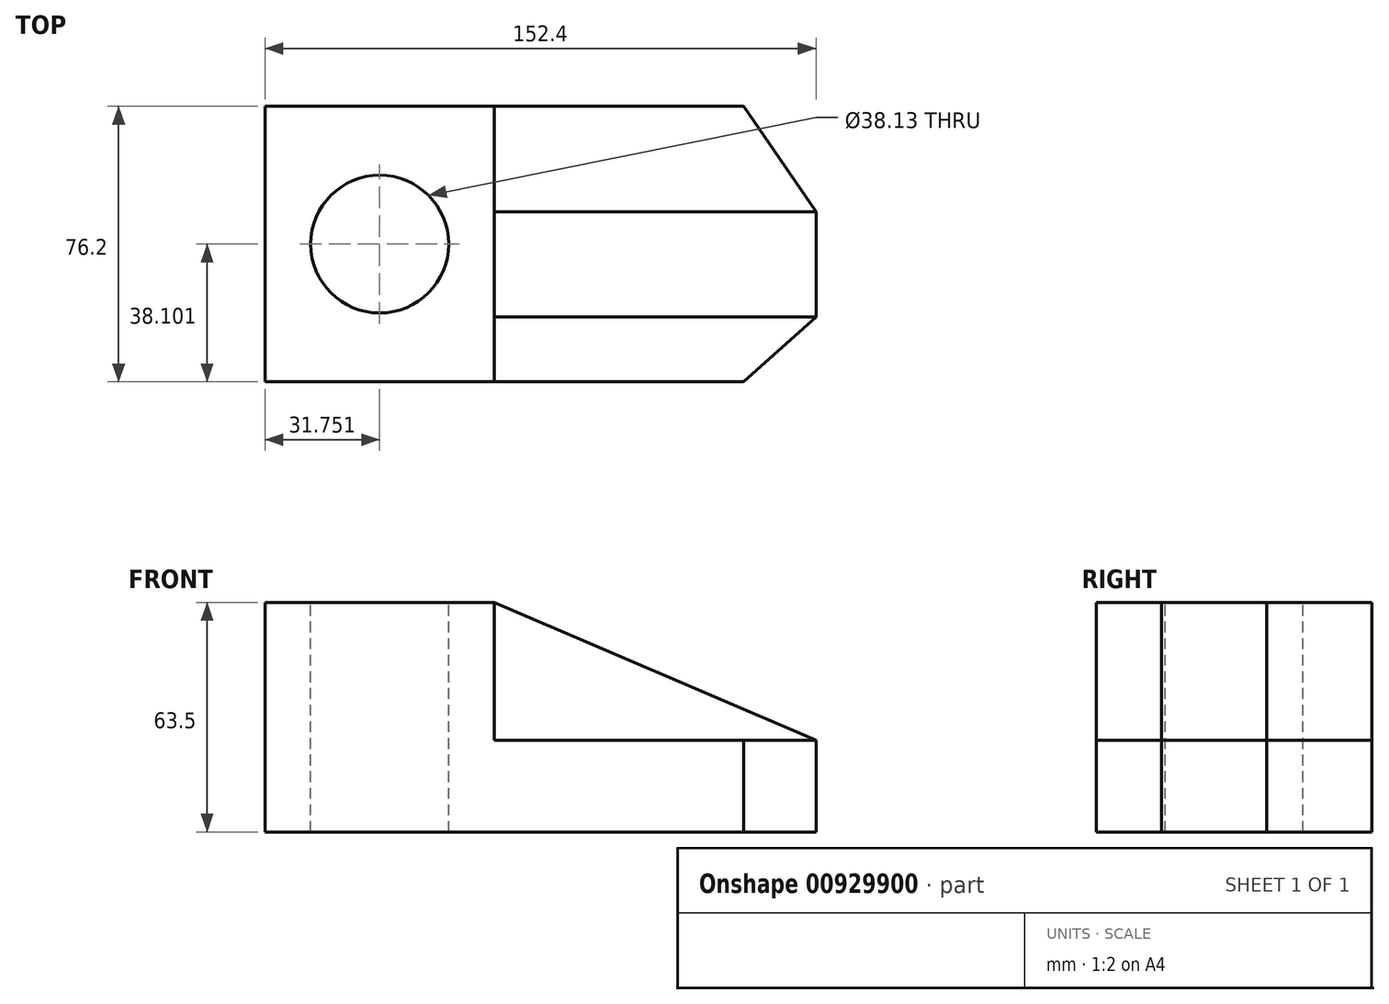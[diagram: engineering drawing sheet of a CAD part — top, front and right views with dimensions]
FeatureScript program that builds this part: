
annotation { "Feature Type Name" : "Feature", "Feature Type Description" : "" }
export const myFeature = defineFeature(function(context is Context, id is Id, definition is map)
    precondition{}
    {
        {
            var Q0;
            Q0=qCreatedBy(makeId("Top.planeOp"),FACE);
            var sketch = newSketch(context, id + "F0", { "sketchPlane" : qUnion([Q0])});
            skLineSegment(sketch, "E0.bottom", {"start": v(-74.87, -28.7) * mm, "end": v(77.53, -28.7) * mm});
            skLineSegment(sketch, "E0.top", {"start": v(-74.87, 47.5) * mm, "end": v(77.53, 47.5) * mm});
            skLineSegment(sketch, "E0.left", {"start": v(-74.87, -28.7) * mm, "end": v(-74.87, 47.5) * mm});
            skLineSegment(sketch, "E0.right", {"start": v(77.53, -28.7) * mm, "end": v(77.53, 47.5) * mm});
            skSolve(sketch);
        }
        {
            var Q0;
            Q0 = qSketchRegion(id + "F0", true);
            extrude(context, id + "F1", {"entities" : qUnion([Q0]), "depth" : 25.4 * mm, "offsetDistance" : 25.4 * mm});
        }
        {
            var Q0;
            Q0=makeQuery(id+"F1.opExtrude","CAP_FACE",FACE,{"disambiguationData":[OSD([sQuery(id+"F0.wireOp",EDGE,"E0.bottom"),sQuery(id+"F0.wireOp",EDGE,"E0.top"),sQuery(id+"F0.wireOp",EDGE,"E0.left"),sQuery(id+"F0.wireOp",EDGE,"E0.right")])],"isStart":false});
            var sketch = newSketch(context, id + "F2", { "sketchPlane" : qUnion([Q0])});
            skLineSegment(sketch, "E1.bottom", {"start": v(-74.87, -28.7) * mm, "end": v(-11.37, -28.7) * mm});
            skLineSegment(sketch, "E1.top", {"start": v(-74.87, 47.5) * mm, "end": v(-11.37, 47.5) * mm});
            skLineSegment(sketch, "E1.left", {"start": v(-74.87, -28.7) * mm, "end": v(-74.87, 47.5) * mm});
            skLineSegment(sketch, "E1.right", {"start": v(-11.37, -28.7) * mm, "end": v(-11.37, 47.5) * mm});
            skSolve(sketch);
        }
        {
            var Q0;
            Q0 = qSketchRegion(id + "F2", true);
            extrude(context, id + "F3", {"entities" : qUnion([Q0]), "operationType" : NewBodyOperationType.ADD, "depth" : 38.1 * mm, "offsetDistance" : 25.4 * mm});
        }
        {
            var Q0;
            Q0=makeQuery(id+"F1.opExtrude","CAP_FACE",FACE,{"disambiguationData":[OSD([sQuery(id+"F0.wireOp",EDGE,"E0.bottom"),sQuery(id+"F0.wireOp",EDGE,"E0.top"),sQuery(id+"F0.wireOp",EDGE,"E0.left"),sQuery(id+"F0.wireOp",EDGE,"E0.right")])],"isStart":false});
            var sketch = newSketch(context, id + "F4", { "sketchPlane" : qUnion([Q0])});
            skLineSegment(sketch, "E2", {"start": v(77.53, -28.7) * mm, "end": v(57.54, -28.7) * mm});
            skLineSegment(sketch, "E3", {"start": v(57.54, -28.7) * mm, "end": v(77.53, -10.72) * mm});
            skLineSegment(sketch, "E4", {"start": v(77.53, -10.72) * mm, "end": v(77.53, -28.7) * mm});
            skSolve(sketch);
        }
        {
            var Q0;
            Q0=makeQuery(id+"F4.imprint","IMPRINT",FACE,{"disambiguationData":[TD([[makeQuery(id+"F4.imprint","IMPRINT",EDGE,{"derivedFrom":sQuery(id+"F4.wireOp",EDGE,"E2")}),1.0]])]});
            extrude(context, id + "F5", {"entities" : qUnion([Q0]), "operationType" : NewBodyOperationType.REMOVE, "oppositeDirection" : true, "depth" : 25.4 * mm, "offsetDistance" : 25.4 * mm});
        }
        {
            var Q0;
            Q0=makeQuery(id+"F1.opExtrude","CAP_FACE",FACE,{"disambiguationData":[OSD([sQuery(id+"F0.wireOp",EDGE,"E0.bottom"),sQuery(id+"F0.wireOp",EDGE,"E0.top"),sQuery(id+"F0.wireOp",EDGE,"E0.left"),sQuery(id+"F0.wireOp",EDGE,"E0.right")])],"isStart":false});
            var sketch = newSketch(context, id + "F6", { "sketchPlane" : qUnion([Q0])});
            skLineSegment(sketch, "E5", {"start": v(57.54, 47.5) * mm, "end": v(77.53, 47.5) * mm});
            skLineSegment(sketch, "E6", {"start": v(77.53, 47.5) * mm, "end": v(77.53, 18.38) * mm});
            skLineSegment(sketch, "E7", {"start": v(77.53, 18.38) * mm, "end": v(57.54, 47.5) * mm});
            skSolve(sketch);
        }
        {
            var Q0;
            Q0 = qSketchRegion(id + "F6", true);
            var Q1;
            Q1=makeQuery(id+"F6.imprint","IMPRINT",FACE,{"disambiguationData":[TD([[makeQuery(id+"F6.imprint","IMPRINT",EDGE,{"derivedFrom":sQuery(id+"F6.wireOp",EDGE,"E5")}),-1.0]])]});
            extrude(context, id + "F7", {"entities" : qUnion([Q0, Q1]), "operationType" : NewBodyOperationType.REMOVE, "oppositeDirection" : true, "depth" : 25.4 * mm, "offsetDistance" : 25.4 * mm});
        }
        {
            var Q0;
            Q0=makeQuery(id+"F1.opExtrude","CAP_FACE",FACE,{"disambiguationData":[OSD([sQuery(id+"F0.wireOp",EDGE,"E0.bottom"),sQuery(id+"F0.wireOp",EDGE,"E0.top"),sQuery(id+"F0.wireOp",EDGE,"E0.left"),sQuery(id+"F0.wireOp",EDGE,"E0.right")])],"isStart":false});
            var sketch = newSketch(context, id + "F8", { "sketchPlane" : qUnion([Q0])});
            skLineSegment(sketch, "E8.bottom", {"start": v(77.53, 18.38) * mm, "end": v(-11.37, 18.38) * mm});
            skLineSegment(sketch, "E8.top", {"start": v(77.53, -10.72) * mm, "end": v(-11.37, -10.72) * mm});
            skLineSegment(sketch, "E8.left", {"start": v(77.53, 18.38) * mm, "end": v(77.53, -10.72) * mm});
            skLineSegment(sketch, "E8.right", {"start": v(-11.37, 18.38) * mm, "end": v(-11.37, -10.72) * mm});
            skSolve(sketch);
        }
        {
            var Q0;
            Q0=makeQuery(id+"F8.imprint","IMPRINT",FACE,{"disambiguationData":[TD([[makeQuery(id+"F8.imprint","IMPRINT",EDGE,{"derivedFrom":sQuery(id+"F8.wireOp",EDGE,"E8.bottom")}),1.0]])]});
            extrude(context, id + "F9", {"entities" : qUnion([Q0]), "operationType" : NewBodyOperationType.ADD, "depth" : 38.1 * mm, "offsetDistance" : 25.4 * mm});
        }
        {
            var Q0;
            Q0=makeQuery(id+"F9.opExtrude","SWEPT_FACE",FACE,{"disambiguationData":[OSD([sQuery(id+"F8.wireOp",EDGE,"E8.top")])]});
            var sketch = newSketch(context, id + "F10", { "sketchPlane" : qUnion([Q0])});
            skLineSegment(sketch, "E9", {"start": v(-11.37, 63.5) * mm, "end": v(77.53, 25.4) * mm});
            skLineSegment(sketch, "E10", {"start": v(77.53, 25.4) * mm, "end": v(77.53, 63.5) * mm});
            skLineSegment(sketch, "E11", {"start": v(77.53, 63.5) * mm, "end": v(-11.37, 63.5) * mm});
            skSolve(sketch);
        }
        {
            var Q0;
            Q0=makeQuery(id+"F10.imprint","IMPRINT",FACE,{"disambiguationData":[TD([[makeQuery(id+"F10.imprint","IMPRINT",EDGE,{"derivedFrom":sQuery(id+"F10.wireOp",EDGE,"E9")}),1.0]])]});
            extrude(context, id + "F11", {"entities" : qUnion([Q0]), "operationType" : NewBodyOperationType.REMOVE, "oppositeDirection" : true, "depth" : 38.1 * mm, "offsetDistance" : 25.4 * mm});
        }
        {
            var Q0;
            Q0=makeQuery(id+"F9.boolean.opBoolean","MERGE",FACE,{"derivedFrom":[makeQuery(id+"F3.opExtrude","CAP_FACE",FACE,{"disambiguationData":[OSD([sQuery(id+"F2.wireOp",EDGE,"E1.bottom"),sQuery(id+"F2.wireOp",EDGE,"E1.top"),sQuery(id+"F2.wireOp",EDGE,"E1.left"),sQuery(id+"F2.wireOp",EDGE,"E1.right")])],"isStart":false}),makeQuery(id+"F9.opExtrude","CAP_FACE",FACE,{"disambiguationData":[OSD([sQuery(id+"F8.wireOp",EDGE,"E8.bottom"),sQuery(id+"F8.wireOp",EDGE,"E8.top"),sQuery(id+"F8.wireOp",EDGE,"E8.left"),sQuery(id+"F8.wireOp",EDGE,"E8.right")])],"isStart":false})]});
            var sketch = newSketch(context, id + "F12", { "sketchPlane" : qUnion([Q0])});
            skCircle(sketch, "E12", {"center": v(-43.12, 9.4) * mm, "radius": 19.06 * mm});
            skPoint(sketch, "E12.centerSnap0", {"position": v(-74.87, 9.4) * mm});
            skPoint(sketch, "E12.centerSnap1", {"position": v(-43.12, -28.7) * mm});
            skSolve(sketch);
        }
        {
            var Q0;
            Q0=makeQuery(id+"F12.imprint","IMPRINT",FACE,{"disambiguationData":[TD([[makeQuery(id+"F12.imprint","IMPRINT",EDGE,{"derivedFrom":sQuery(id+"F12.wireOp",EDGE,"E12")}),1.0]])]});
            extrude(context, id + "F13", {"entities" : qUnion([Q0]), "operationType" : NewBodyOperationType.REMOVE, "oppositeDirection" : true, "depth" : 76.2 * mm, "offsetDistance" : 25.4 * mm});
        }
    });
